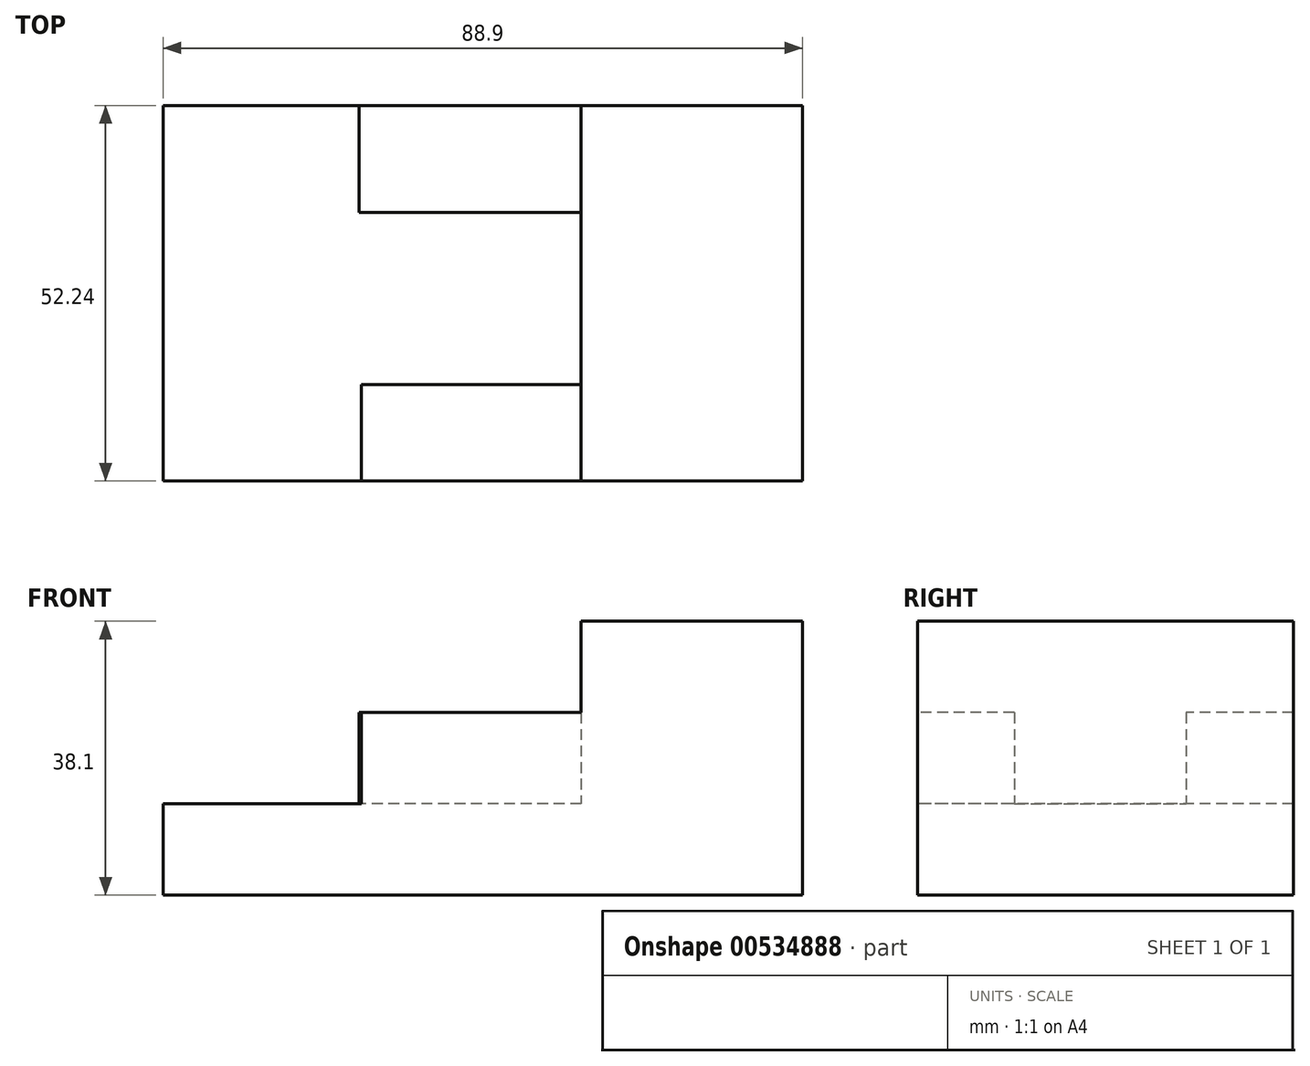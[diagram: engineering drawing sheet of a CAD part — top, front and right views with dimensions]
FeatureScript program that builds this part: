
annotation { "Feature Type Name" : "Feature", "Feature Type Description" : "" }
export const myFeature = defineFeature(function(context is Context, id is Id, definition is map)
    precondition{}
    {
        {
            var Q0;
            Q0=qCreatedBy(makeId("Top.planeOp"),FACE);
            var sketch = newSketch(context, id + "F0", { "sketchPlane" : qUnion([Q0])});
            skLineSegment(sketch, "E0.bottom", {"start": v(-44.45, 26.12) * mm, "end": v(44.45, 26.12) * mm});
            skLineSegment(sketch, "E0.top", {"start": v(-44.45, -26.12) * mm, "end": v(44.45, -26.12) * mm});
            skLineSegment(sketch, "E0.left", {"start": v(-44.45, 26.12) * mm, "end": v(-44.45, -26.12) * mm});
            skLineSegment(sketch, "E0.right", {"start": v(44.45, 26.12) * mm, "end": v(44.45, -26.12) * mm});
            skPoint(sketch, "E0.middle", {"position": v(0, 0) * mm});
            skSolve(sketch);
        }
        {
            var Q0;
            Q0 = qSketchRegion(id + "F0", true);
            extrude(context, id + "F1", {"entities" : qUnion([Q0]), "depth" : 12.7 * mm, "offsetDistance" : 25.4 * mm});
        }
        {
            var Q0;
            Q0=makeQuery(id+"F1.opExtrude","CAP_FACE",FACE,{"disambiguationData":[OSD([sQuery(id+"F0.wireOp",EDGE,"E0.bottom"),sQuery(id+"F0.wireOp",EDGE,"E0.top"),sQuery(id+"F0.wireOp",EDGE,"E0.left"),sQuery(id+"F0.wireOp",EDGE,"E0.right")])],"isStart":false});
            var sketch = newSketch(context, id + "F2", { "sketchPlane" : qUnion([Q0])});
            skLineSegment(sketch, "E1.bottom", {"start": v(-17.2, 26.12) * mm, "end": v(44.45, 26.12) * mm});
            skLineSegment(sketch, "E1.top", {"start": v(-17.2, 11.22) * mm, "end": v(13.68, 11.22) * mm});
            skLineSegment(sketch, "E1.left", {"start": v(-17.2, 26.12) * mm, "end": v(-17.2, 11.22) * mm});
            skLineSegment(sketch, "E1.right", {"start": v(44.45, 26.12) * mm, "end": v(44.45, 11.22) * mm});
            skLineSegment(sketch, "E2.bottom", {"start": v(13.68, -12.68) * mm, "end": v(-16.9, -12.68) * mm});
            skLineSegment(sketch, "E2.top", {"start": v(44.45, -26.12) * mm, "end": v(-16.9, -26.12) * mm});
            skLineSegment(sketch, "E2.left", {"start": v(44.45, -12.68) * mm, "end": v(44.45, -26.12) * mm});
            skLineSegment(sketch, "E2.right", {"start": v(-16.9, -12.68) * mm, "end": v(-16.9, -26.12) * mm});
            skLineSegment(sketch, "E3.left", {"start": v(13.68, -12.68) * mm, "end": v(13.68, 11.22) * mm});
            skLineSegment(sketch, "E3.right", {"start": v(44.45, -12.68) * mm, "end": v(44.45, 11.22) * mm});
            skLineSegment(sketch, "E4", {"start": v(13.68, 11.22) * mm, "end": v(13.68, 26.12) * mm});
            skLineSegment(sketch, "E5", {"start": v(13.68, 26.12) * mm, "end": v(13.68, -12.68) * mm});
            skLineSegment(sketch, "E6", {"start": v(13.68, -12.68) * mm, "end": v(13.68, -26.12) * mm});
            skSolve(sketch);
        }
        {
            var Q0;
            {var subQ4=sQuery(id+"F2.wireOp",EDGE,"E1.top");Q0=makeQuery(id+"F2.imprint","IMPRINT",FACE,{"disambiguationData":[TD([[makeQuery(id+"F2.imprint","IMPRINT",EDGE,{"derivedFrom":subQ4}),1.0]])]});}
            var Q1;
            Q1=makeQuery(id+"F2.imprint","IMPRINT",FACE,{"disambiguationData":[TD([[makeQuery(id+"F2.imprint","IMPRINT",EDGE,{"derivedFrom":sQuery(id+"F2.wireOp",EDGE,"E2.bottom")}),1.0]])]});
            extrude(context, id + "F3", {"entities" : qUnion([Q0, Q1]), "operationType" : NewBodyOperationType.ADD, "depth" : 12.7 * mm, "offsetDistance" : 25.4 * mm});
        }
        {
            var Q0;
            {var subQ3=sQuery(id+"F2.wireOp",EDGE,"E1.right");Q0=makeQuery(id+"F2.imprint","IMPRINT",FACE,{"disambiguationData":[TD([[makeQuery(id+"F2.imprint","IMPRINT",EDGE,{"derivedFrom":subQ3}),-1.0]])]});}
            extrude(context, id + "F4", {"entities" : qUnion([Q0]), "operationType" : NewBodyOperationType.ADD, "depth" : 25.4 * mm, "offsetDistance" : 25.4 * mm});
        }
    });
